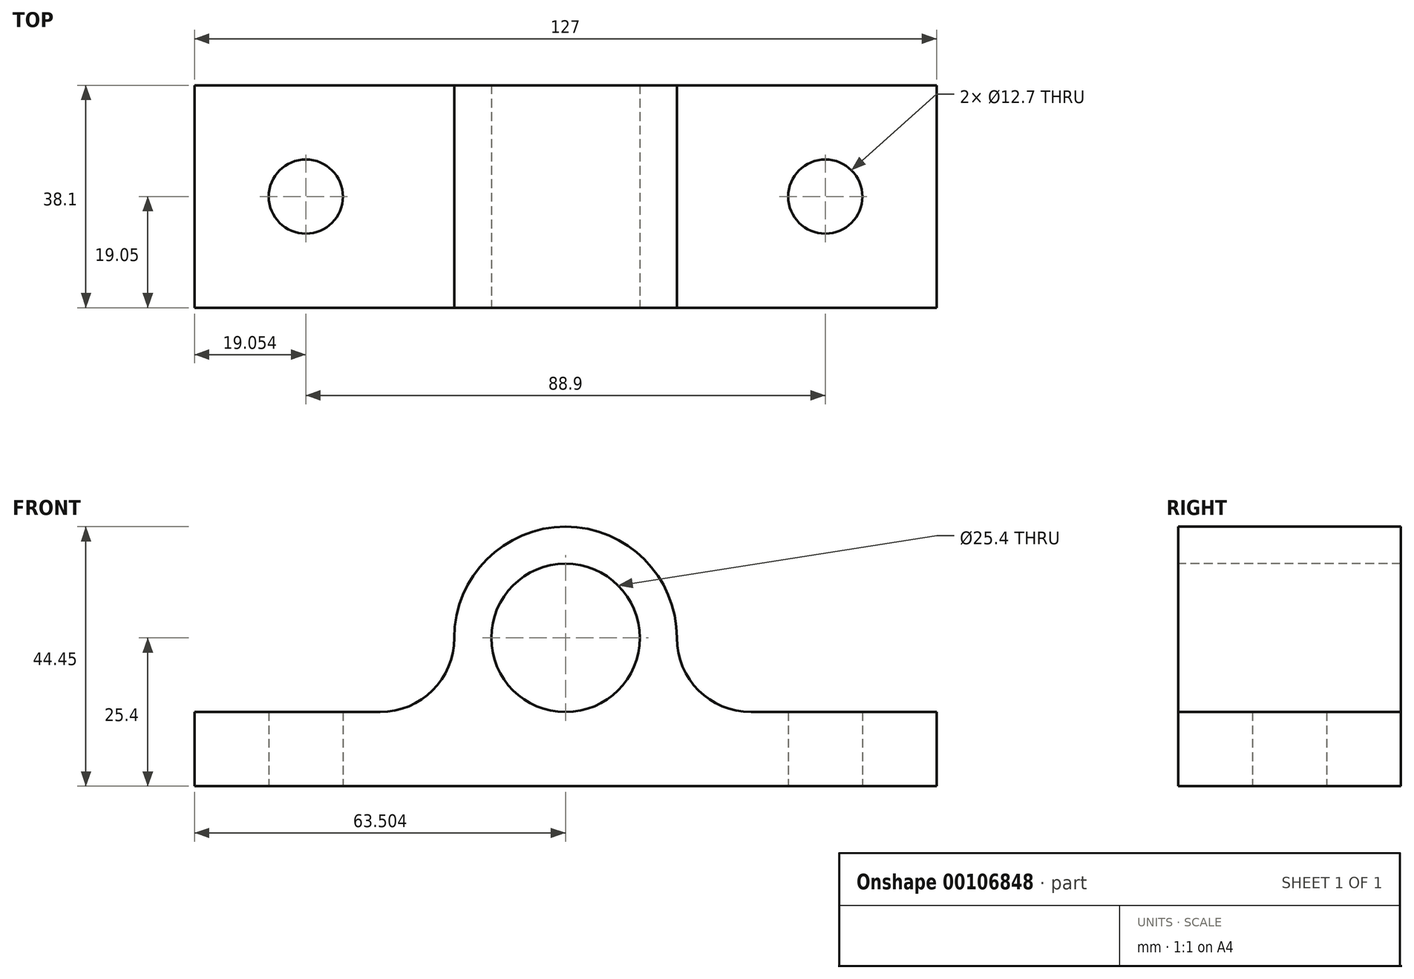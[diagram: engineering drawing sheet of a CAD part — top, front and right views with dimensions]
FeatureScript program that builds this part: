
annotation { "Feature Type Name" : "Feature", "Feature Type Description" : "" }
export const myFeature = defineFeature(function(context is Context, id is Id, definition is map)
    precondition{}
    {
        {
            var Q0;
            Q0=qCreatedBy(makeId("Front.planeOp"),FACE);
            var sketch = newSketch(context, id + "F0", { "sketchPlane" : qUnion([Q0])});
            skLineSegment(sketch, "E0", {"start": v(-39.82, 0) * mm, "end": v(87.18, 0) * mm});
            skLineSegment(sketch, "E1", {"start": v(87.18, 0) * mm, "end": v(87.18, 12.7) * mm});
            skLineSegment(sketch, "E2", {"start": v(-39.82, 12.7) * mm, "end": v(-39.82, 0) * mm});
            skPoint(sketch, "E3.newPointB", {"position": v(-39.82, 12.7) * mm});
            skCircle(sketch, "E4", {"center": v(23.68, 25.4) * mm, "radius": 12.7 * mm});
            skLineSegment(sketch, "E5", {"start": v(42.73, 25.4) * mm, "end": v(42.73, 43.66) * mm});
            skLineSegment(sketch, "E6", {"start": v(55.43, 12.7) * mm, "end": v(87.18, 12.7) * mm});
            skLineSegment(sketch, "E7", {"start": v(-39.82, 12.7) * mm, "end": v(-8.07, 12.7) * mm});
            skLineSegment(sketch, "E8", {"start": v(4.63, 25.4) * mm, "end": v(4.63, 43.66) * mm});
            skPoint(sketch, "E9.visualSharp", {"position": v(42.73, 12.7) * mm});
            skArc(sketch, "E9.filletArc", {"start": v(42.73, 25.4) * mm, "mid": v(46.45, 16.42) * mm, "end": v(55.43, 12.7) * mm});
            skPoint(sketch, "E10.visualSharp", {"position": v(4.63, 12.7) * mm});
            skArc(sketch, "E10.filletArc", {"start": v(-8.07, 12.7) * mm, "mid": v(0.91, 16.42) * mm, "end": v(4.63, 25.4) * mm});
            skLineSegment(sketch, "E11", {"start": v(23.68, 25.4) * mm, "end": v(23.68, 0) * mm, "construction": true});
            skArc(sketch, "E12", {"start": v(42.73, 25.4) * mm, "mid": v(23.68, 44.45) * mm, "end": v(4.63, 25.4) * mm});
            skSolve(sketch);
        }
        {
            var Q0;
            {var subQ4=sQuery(id+"F0.wireOp",EDGE,"E1");Q0=makeQuery(id+"F0.imprint","IMPRINT",FACE,{"disambiguationData":[TD([[makeQuery(id+"F0.imprint","IMPRINT",EDGE,{"derivedFrom":subQ4}),1.0]])]});}
            var Q1;
            {var subQ0=sQuery(id+"F0.wireOp",EDGE,"KekfI1T5-vIR2-GzC9-LNCg-jJF9AiQaI8wj");Q1=makeQuery(id+"F0.imprint","IMPRINT",FACE,{"disambiguationData":[TD([[makeQuery(id+"F0.imprint","IMPRINT",EDGE,{"derivedFrom":subQ0}),1.0]])]});}
            var Q2;
            {var subQ0=sQuery(id+"F0.wireOp",EDGE,"E2");Q2=makeQuery(id+"F0.imprint","IMPRINT",FACE,{"disambiguationData":[TD([[makeQuery(id+"F0.imprint","IMPRINT",EDGE,{"derivedFrom":subQ0}),1.0]])]});}
            extrude(context, id + "F1", {"entities" : qUnion([Q0, Q1, Q2]), "oppositeDirection" : true, "depth" : 38.1 * mm});
        }
        {
            var Q0;
            Q0=qCreatedBy(makeId("Top.planeOp"),FACE);
            var sketch = newSketch(context, id + "F2", { "sketchPlane" : qUnion([Q0])});
            skCircle(sketch, "E13", {"center": v(-20.77, 19.05) * mm, "radius": 6.35 * mm});
            skCircle(sketch, "E14", {"center": v(68.13, 19.05) * mm, "radius": 6.35 * mm});
            skSolve(sketch);
        }
        {
            var Q0;
            Q0 = qSketchRegion(id + "F2", true);
            extrude(context, id + "F3", {"entities" : qUnion([Q0]), "operationType" : NewBodyOperationType.REMOVE, "depth" : 25.4 * mm});
        }
    });
